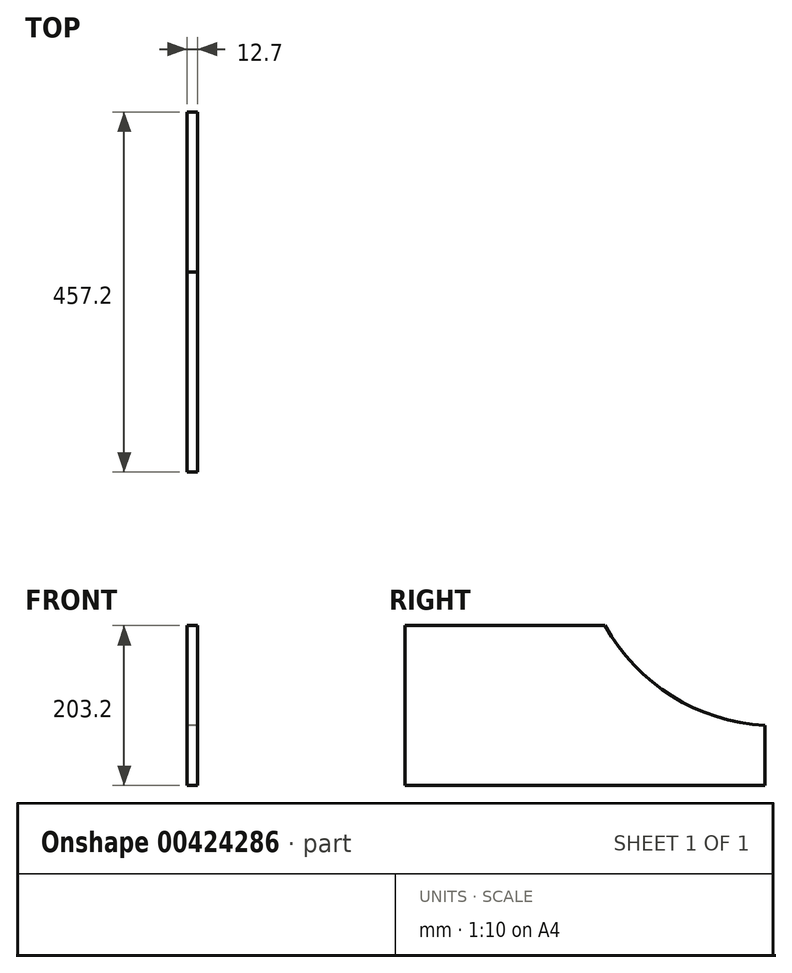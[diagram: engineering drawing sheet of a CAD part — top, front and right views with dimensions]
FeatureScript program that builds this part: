
annotation { "Feature Type Name" : "Feature", "Feature Type Description" : "" }
export const myFeature = defineFeature(function(context is Context, id is Id, definition is map)
    precondition{}
    {
        {
            var Q0;
            Q0=qCreatedBy(makeId("Right.planeOp"),FACE);
            var sketch = newSketch(context, id + "F0", { "sketchPlane" : qUnion([Q0])});
            skLineSegment(sketch, "E0.bottom", {"start": v(-222.33, 36.25) * mm, "end": v(234.87, 36.25) * mm});
            skLineSegment(sketch, "E0.top", {"start": v(-222.33, -166.95) * mm, "end": v(234.87, -166.95) * mm});
            skLineSegment(sketch, "E0.left", {"start": v(-222.33, 36.25) * mm, "end": v(-222.33, -166.95) * mm});
            skLineSegment(sketch, "E0.right", {"start": v(234.87, 36.25) * mm, "end": v(234.87, -166.95) * mm});
            skArc(sketch, "E1", {"start": v(31.67, 36.25) * mm, "mid": v(116.92, -53.42) * mm, "end": v(234.87, -90.75) * mm});
            skSolve(sketch);
        }
        {
            var Q0;
            {var subQ1=sQuery(id+"F0.wireOp",EDGE,"E0.top");Q0=makeQuery(id+"F0.imprint","IMPRINT",FACE,{"disambiguationData":[TD([[makeQuery(id+"F0.imprint","IMPRINT",EDGE,{"derivedFrom":subQ1}),1.0]])]});}
            extrude(context, id + "F1", {"entities" : qUnion([Q0]), "depth" : 12.7 * mm});
        }
    });
